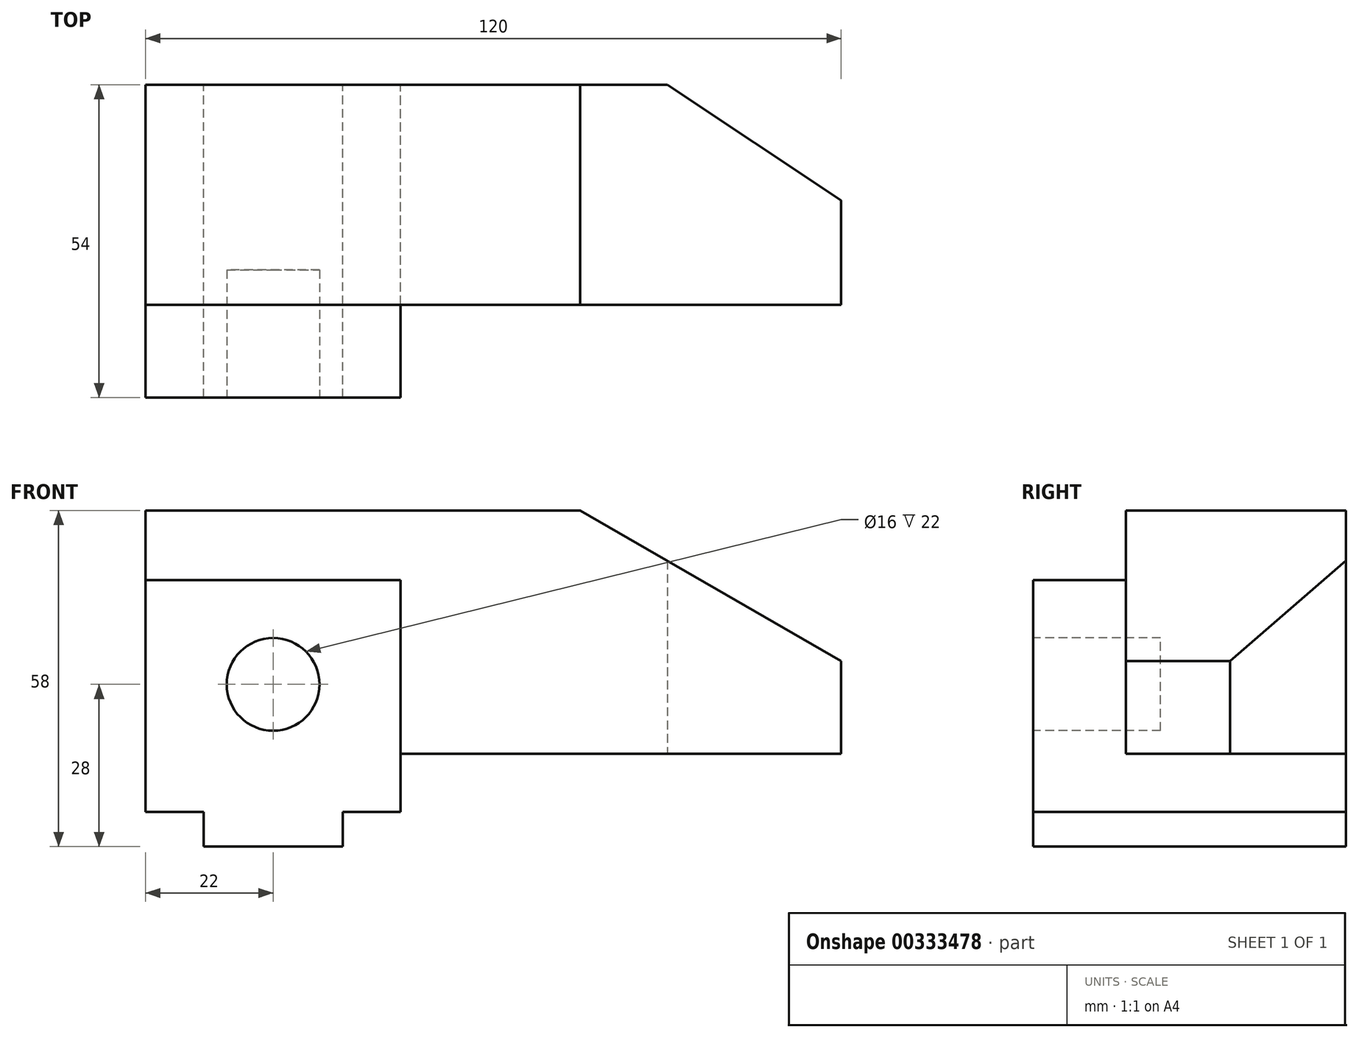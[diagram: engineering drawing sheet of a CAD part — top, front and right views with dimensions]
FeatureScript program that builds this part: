
annotation { "Feature Type Name" : "Feature", "Feature Type Description" : "" }
export const myFeature = defineFeature(function(context is Context, id is Id, definition is map)
    precondition{}
    {
        {
            var Q0;
            Q0=qCreatedBy(makeId("Front.planeOp"),FACE);
            var sketch = newSketch(context, id + "F0", { "sketchPlane" : qUnion([Q0])});
            skLineSegment(sketch, "E0", {"start": v(0, 0) * mm, "end": v(0, 6) * mm});
            skLineSegment(sketch, "E1", {"start": v(0, 6) * mm, "end": v(-10, 6) * mm});
            skLineSegment(sketch, "E2", {"start": v(-10, 6) * mm, "end": v(-10, 58) * mm});
            skLineSegment(sketch, "E3", {"start": v(-10, 58) * mm, "end": v(65, 58) * mm});
            skLineSegment(sketch, "E4", {"start": v(65, 58) * mm, "end": v(110, 32.02) * mm});
            skLineSegment(sketch, "E5", {"start": v(110, 32.02) * mm, "end": v(110, 16) * mm});
            skLineSegment(sketch, "E6", {"start": v(110, 16) * mm, "end": v(34, 16) * mm});
            skLineSegment(sketch, "E7", {"start": v(34, 16) * mm, "end": v(34, 6) * mm});
            skLineSegment(sketch, "E8", {"start": v(34, 6) * mm, "end": v(24, 6) * mm});
            skLineSegment(sketch, "E9", {"start": v(24, 6) * mm, "end": v(24, 0) * mm});
            skLineSegment(sketch, "E10", {"start": v(24, 0) * mm, "end": v(0, 0) * mm});
            skSolve(sketch);
        }
        {
            var Q0;
            Q0=makeQuery(id+"F0.imprint","IMPRINT",FACE,{"disambiguationData":[TD([[makeQuery(id+"F0.imprint","IMPRINT",EDGE,{"derivedFrom":sQuery(id+"F0.wireOp",EDGE,"E0")}),-1.0]])]});
            extrude(context, id + "F1", {"entities" : qUnion([Q0]), "depth" : 54 * mm});
        }
        {
            var Q0;
            Q0=makeQuery(id+"F1.opExtrude","CAP_FACE",FACE,{"disambiguationData":[OSD([sQuery(id+"F0.wireOp",EDGE,"E0"),sQuery(id+"F0.wireOp",EDGE,"E1"),sQuery(id+"F0.wireOp",EDGE,"E2"),sQuery(id+"F0.wireOp",EDGE,"E3"),sQuery(id+"F0.wireOp",EDGE,"E4"),sQuery(id+"F0.wireOp",EDGE,"E5"),sQuery(id+"F0.wireOp",EDGE,"E6"),sQuery(id+"F0.wireOp",EDGE,"E7"),sQuery(id+"F0.wireOp",EDGE,"E8"),sQuery(id+"F0.wireOp",EDGE,"E9"),sQuery(id+"F0.wireOp",EDGE,"E10")])],"isStart":false});
            var sketch = newSketch(context, id + "F2", { "sketchPlane" : qUnion([Q0])});
            skLineSegment(sketch, "E11", {"start": v(-10, 58) * mm, "end": v(65, 58) * mm});
            skLineSegment(sketch, "E12", {"start": v(65, 58) * mm, "end": v(110, 32.02) * mm});
            skLineSegment(sketch, "E13", {"start": v(110, 32.02) * mm, "end": v(110, 16) * mm});
            skLineSegment(sketch, "E14", {"start": v(110, 16) * mm, "end": v(34, 16) * mm});
            skLineSegment(sketch, "E15", {"start": v(34, 16) * mm, "end": v(34, 46) * mm});
            skLineSegment(sketch, "E16", {"start": v(34, 46) * mm, "end": v(-10, 46) * mm});
            skLineSegment(sketch, "E17", {"start": v(-10, 46) * mm, "end": v(-10, 58) * mm});
            skSolve(sketch);
        }
        {
            var Q0;
            Q0=makeQuery(id+"F2.imprint","IMPRINT",FACE,{"disambiguationData":[TD([[makeQuery(id+"F2.imprint","IMPRINT",EDGE,{"derivedFrom":sQuery(id+"F2.wireOp",EDGE,"E11")}),-1.0]])]});
            extrude(context, id + "F3", {"entities" : qUnion([Q0]), "operationType" : NewBodyOperationType.REMOVE, "oppositeDirection" : true, "depth" : 16 * mm});
        }
        {
            var Q0;
            Q0=makeQuery(id+"F1.opExtrude","CAP_FACE",FACE,{"disambiguationData":[OSD([sQuery(id+"F0.wireOp",EDGE,"E0"),sQuery(id+"F0.wireOp",EDGE,"E1"),sQuery(id+"F0.wireOp",EDGE,"E2"),sQuery(id+"F0.wireOp",EDGE,"E3"),sQuery(id+"F0.wireOp",EDGE,"E4"),sQuery(id+"F0.wireOp",EDGE,"E5"),sQuery(id+"F0.wireOp",EDGE,"E6"),sQuery(id+"F0.wireOp",EDGE,"E7"),sQuery(id+"F0.wireOp",EDGE,"E8"),sQuery(id+"F0.wireOp",EDGE,"E9"),sQuery(id+"F0.wireOp",EDGE,"E10")])],"isStart":false});
            var sketch = newSketch(context, id + "F4", { "sketchPlane" : qUnion([Q0])});
            skCircle(sketch, "E18", {"center": v(12, 28) * mm, "radius": 8 * mm});
            skSolve(sketch);
        }
        {
            var Q0;
            Q0=makeQuery(id+"F4.imprint","IMPRINT",FACE,{"disambiguationData":[TD([[makeQuery(id+"F4.imprint","IMPRINT",EDGE,{"derivedFrom":sQuery(id+"F4.wireOp",EDGE,"E18")}),1.0]])]});
            extrude(context, id + "F5", {"entities" : qUnion([Q0]), "operationType" : NewBodyOperationType.REMOVE, "oppositeDirection" : true, "depth" : 22 * mm});
        }
        {
            var Q0;
            Q0=makeQuery(id+"F1.opExtrude","SWEPT_FACE",FACE,{"disambiguationData":[OSD([sQuery(id+"F0.wireOp",EDGE,"E6")])]});
            var sketch = newSketch(context, id + "F6", { "sketchPlane" : qUnion([Q0])});
            skLineSegment(sketch, "E19", {"start": v(80, 0) * mm, "end": v(110, 20) * mm});
            skLineSegment(sketch, "E20", {"start": v(110, 20) * mm, "end": v(110, 0) * mm});
            skLineSegment(sketch, "E21", {"start": v(110, 0) * mm, "end": v(80, 0) * mm});
            skSolve(sketch);
        }
        {
            var Q0;
            Q0=makeQuery(id+"F6.imprint","IMPRINT",FACE,{"disambiguationData":[TD([[makeQuery(id+"F6.imprint","IMPRINT",EDGE,{"derivedFrom":sQuery(id+"F6.wireOp",EDGE,"E19")}),-1.0]])]});
            extrude(context, id + "F7", {"entities" : qUnion([Q0]), "operationType" : NewBodyOperationType.REMOVE, "endBound" : BoundingType.THROUGH_ALL, "oppositeDirection" : true, "depth" : 25 * mm});
        }
    });
